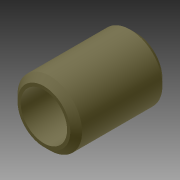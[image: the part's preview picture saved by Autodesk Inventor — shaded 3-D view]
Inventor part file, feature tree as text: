
AUTODESK INVENTOR PART (.ipt)
format: ipt  version: 2014 (Build 180170000, 170)  size: 119,296 bytes
history: native  units: in
note: dims shown in document units (in); Inventor stores cm internally (conversion verified against a paired STEP export)
features: other x35, revolve x1, sketch x1
ambient origin geometry x8: Origin, YZ Plane, XZ Plane, XY Plane, X Axis, Y Axis, Z Axis, Center Point
bodies: Solid1 (feature_tree)
feature tree (37):
  revolve  "Revolution1"  [1 undecoded]
  other  "bushing_XY"
  other  "bushing_YZ"
  other  "bushing_ZX"
  other  "bushing_X"
  other  "bushing_Y"
  other  "bushing_Z"
  other  "bushing_Center"
  other  "id1_XY"
  other  "id1_YZ"
  other  "id1_ZX"
  other  "id1_X"
  other  "id1_Y"
  other  "id1_Z"
  other  "id1_Center"
  other  "id2_XY"
  other  "id2_YZ"
  other  "id2_ZX"
  other  "id2_X"
  other  "id2_Y"
  other  "id2_Z"
  other  "id2_Center"
  other  "id3_XY"
  other  "id3_YZ"
  other  "id3_ZX"
  other  "id3_X"
  other  "id3_Y"
  other  "id3_Z"
  other  "id3_Center"
  other  "id4_XY"
  other  "id4_YZ"
  other  "id4_ZX"
  other  "id4_X"
  other  "id4_Y"
  other  "id4_Z"
  other  "id4_Center"
  sketch  "Sketch_1"  dims[d0=360.0deg]
note: 1 required parameter value undecoded (feature->parameter linkage not recoverable at this tier; creation-order binding heuristic only, values carry confidence <= 0.55)
